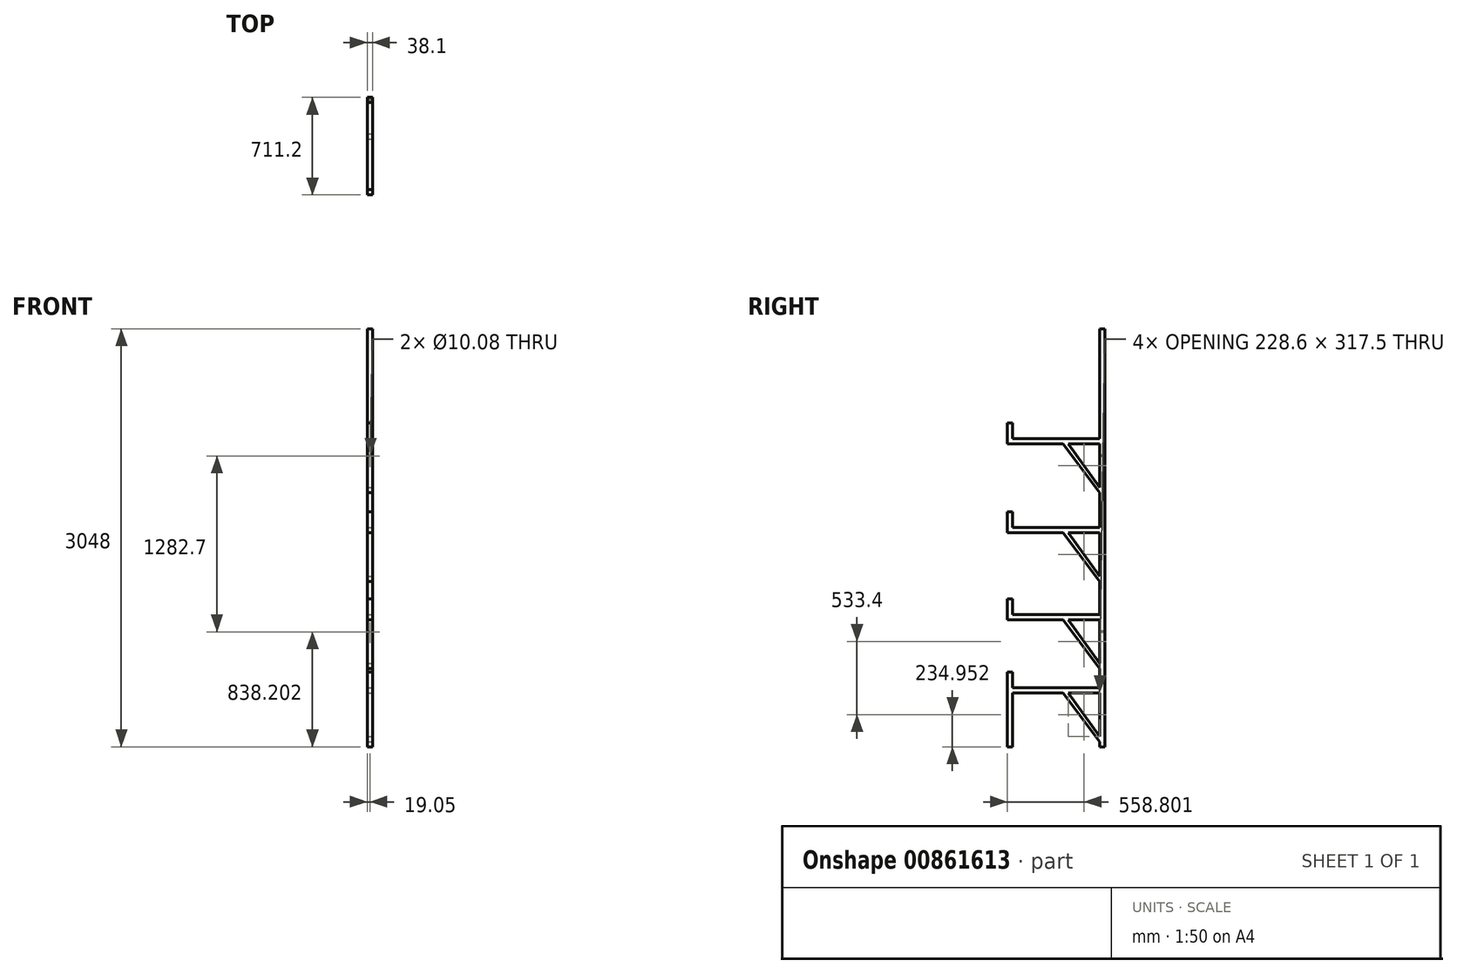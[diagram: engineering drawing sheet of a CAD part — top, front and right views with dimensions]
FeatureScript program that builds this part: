
annotation { "Feature Type Name" : "Feature", "Feature Type Description" : "" }
export const myFeature = defineFeature(function(context is Context, id is Id, definition is map)
    precondition{}
    {
        {
            var Q0;
            Q0=qCreatedBy(makeId("Right.planeOp"),FACE);
            var sketch = newSketch(context, id + "F0", { "sketchPlane" : qUnion([Q0])});
            skLineSegment(sketch, "E0.bottom", {"start": v(-10.09, 2961.46) * mm, "end": v(28.01, 2961.46) * mm});
            skLineSegment(sketch, "E0.top", {"start": v(-10.09, -86.54) * mm, "end": v(28.01, -86.54) * mm});
            skLineSegment(sketch, "E0.left", {"start": v(-10.09, 2961.46) * mm, "end": v(-10.09, -86.54) * mm});
            skLineSegment(sketch, "E0.right", {"start": v(28.01, 2961.46) * mm, "end": v(28.01, -86.54) * mm});
            skSolve(sketch);
        }
        {
            var Q0;
            Q0 = qSketchRegion(id + "F0", true);
            extrude(context, id + "F1", {"entities" : qUnion([Q0]), "depth" : 38.1 * mm, "offsetDistance" : 25.4 * mm});
        }
        {
            var Q0;
            Q0=makeQuery(id+"F1.opExtrude","SWEPT_FACE",FACE,{"disambiguationData":[OSD([sQuery(id+"F0.wireOp",EDGE,"E0.left")])]});
            var sketch = newSketch(context, id + "F2", { "sketchPlane" : qUnion([Q0])});
            skLineSegment(sketch, "E1.bottom", {"start": v(0, 2161.36) * mm, "end": v(38.1, 2161.36) * mm});
            skLineSegment(sketch, "E1.top", {"start": v(0, 2123.26) * mm, "end": v(38.1, 2123.26) * mm});
            skLineSegment(sketch, "E1.left", {"start": v(0, 2161.36) * mm, "end": v(0, 2123.26) * mm});
            skLineSegment(sketch, "E1.right", {"start": v(38.1, 2161.36) * mm, "end": v(38.1, 2123.26) * mm});
            skLineSegment(sketch, "E2.bottom", {"start": v(0, 1513.66) * mm, "end": v(38.1, 1513.66) * mm});
            skLineSegment(sketch, "E2.top", {"start": v(0, 1475.56) * mm, "end": v(38.1, 1475.56) * mm});
            skLineSegment(sketch, "E2.left", {"start": v(0, 1513.66) * mm, "end": v(0, 1475.56) * mm});
            skLineSegment(sketch, "E2.right", {"start": v(38.1, 1513.66) * mm, "end": v(38.1, 1475.56) * mm});
            skLineSegment(sketch, "E3.bottom", {"start": v(0, 878.66) * mm, "end": v(38.1, 878.66) * mm});
            skLineSegment(sketch, "E3.top", {"start": v(0, 840.56) * mm, "end": v(38.1, 840.56) * mm});
            skLineSegment(sketch, "E3.left", {"start": v(0, 878.66) * mm, "end": v(0, 840.56) * mm});
            skLineSegment(sketch, "E3.right", {"start": v(38.1, 878.66) * mm, "end": v(38.1, 840.56) * mm});
            skLineSegment(sketch, "E4.bottom", {"start": v(0, 345.26) * mm, "end": v(38.1, 345.26) * mm});
            skLineSegment(sketch, "E4.top", {"start": v(0, 307.16) * mm, "end": v(38.1, 307.16) * mm});
            skLineSegment(sketch, "E4.left", {"start": v(0, 345.26) * mm, "end": v(0, 307.16) * mm});
            skLineSegment(sketch, "E4.right", {"start": v(38.1, 345.26) * mm, "end": v(38.1, 307.16) * mm});
            skSolve(sketch);
        }
        {
            var Q0;
            Q0 = qSketchRegion(id + "F2", true);
            extrude(context, id + "F3", {"entities" : qUnion([Q0]), "operationType" : NewBodyOperationType.ADD, "depth" : 673.1 * mm, "offsetDistance" : 25.4 * mm});
        }
        {
            var Q0;
            Q0=makeQuery(id+"F3.opExtrude","SWEPT_FACE",FACE,{"disambiguationData":[OSD([sQuery(id+"F2.wireOp",EDGE,"E1.bottom")])]});
            var sketch = newSketch(context, id + "F4", { "sketchPlane" : qUnion([Q0])});
            skLineSegment(sketch, "E5.bottom", {"start": v(38.1, -683.19) * mm, "end": v(0, -683.19) * mm});
            skLineSegment(sketch, "E5.top", {"start": v(38.1, -645.09) * mm, "end": v(0, -645.09) * mm});
            skLineSegment(sketch, "E5.left", {"start": v(38.1, -683.19) * mm, "end": v(38.1, -645.09) * mm});
            skLineSegment(sketch, "E5.right", {"start": v(0, -683.19) * mm, "end": v(0, -645.09) * mm});
            skSolve(sketch);
        }
        {
            var Q0;
            Q0 = qSketchRegion(id + "F4", true);
            extrude(context, id + "F5", {"entities" : qUnion([Q0]), "operationType" : NewBodyOperationType.ADD, "depth" : 114.3 * mm, "offsetDistance" : 25.4 * mm});
        }
        {
            var Q0;
            Q0=makeQuery(id+"F3.opExtrude","SWEPT_FACE",FACE,{"disambiguationData":[OSD([sQuery(id+"F2.wireOp",EDGE,"E2.bottom")])]});
            var sketch = newSketch(context, id + "F6", { "sketchPlane" : qUnion([Q0])});
            skLineSegment(sketch, "E6.bottom", {"start": v(38.1, -683.19) * mm, "end": v(0, -683.19) * mm});
            skLineSegment(sketch, "E6.top", {"start": v(38.1, -645.09) * mm, "end": v(0, -645.09) * mm});
            skLineSegment(sketch, "E6.left", {"start": v(38.1, -683.19) * mm, "end": v(38.1, -645.09) * mm});
            skLineSegment(sketch, "E6.right", {"start": v(0, -683.19) * mm, "end": v(0, -645.09) * mm});
            skSolve(sketch);
        }
        {
            var Q0;
            Q0 = qSketchRegion(id + "F6", true);
            extrude(context, id + "F7", {"entities" : qUnion([Q0]), "operationType" : NewBodyOperationType.ADD, "depth" : 114.3 * mm, "offsetDistance" : 25.4 * mm});
        }
        {
            var Q0;
            Q0=makeQuery(id+"F3.opExtrude","SWEPT_FACE",FACE,{"disambiguationData":[OSD([sQuery(id+"F2.wireOp",EDGE,"E3.bottom")])]});
            var sketch = newSketch(context, id + "F8", { "sketchPlane" : qUnion([Q0])});
            skLineSegment(sketch, "E7.bottom", {"start": v(38.1, -683.19) * mm, "end": v(0, -683.19) * mm});
            skLineSegment(sketch, "E7.top", {"start": v(38.1, -645.09) * mm, "end": v(0, -645.09) * mm});
            skLineSegment(sketch, "E7.left", {"start": v(38.1, -683.19) * mm, "end": v(38.1, -645.09) * mm});
            skLineSegment(sketch, "E7.right", {"start": v(0, -683.19) * mm, "end": v(0, -645.09) * mm});
            skSolve(sketch);
        }
        {
            var Q0;
            Q0 = qSketchRegion(id + "F8", true);
            extrude(context, id + "F9", {"entities" : qUnion([Q0]), "operationType" : NewBodyOperationType.ADD, "depth" : 114.3 * mm, "offsetDistance" : 25.4 * mm});
        }
        {
            var Q0;
            Q0=makeQuery(id+"F3.opExtrude","SWEPT_FACE",FACE,{"disambiguationData":[OSD([sQuery(id+"F2.wireOp",EDGE,"E4.bottom")])]});
            var sketch = newSketch(context, id + "F10", { "sketchPlane" : qUnion([Q0])});
            skLineSegment(sketch, "E8.bottom", {"start": v(38.1, -683.19) * mm, "end": v(0, -683.19) * mm});
            skLineSegment(sketch, "E8.top", {"start": v(38.1, -645.09) * mm, "end": v(0, -645.09) * mm});
            skLineSegment(sketch, "E8.left", {"start": v(38.1, -683.19) * mm, "end": v(38.1, -645.09) * mm});
            skLineSegment(sketch, "E8.right", {"start": v(0, -683.19) * mm, "end": v(0, -645.09) * mm});
            skSolve(sketch);
        }
        {
            var Q0;
            Q0 = qSketchRegion(id + "F10", true);
            extrude(context, id + "F11", {"entities" : qUnion([Q0]), "operationType" : NewBodyOperationType.ADD, "depth" : 114.3 * mm, "offsetDistance" : 25.4 * mm});
        }
        {
            var Q0;
            Q0=makeQuery(id+"F3.opExtrude","SWEPT_FACE",FACE,{"disambiguationData":[OSD([sQuery(id+"F2.wireOp",EDGE,"E4.top")])]});
            var sketch = newSketch(context, id + "F12", { "sketchPlane" : qUnion([Q0])});
            skLineSegment(sketch, "E9.bottom", {"start": v(38.1, 683.19) * mm, "end": v(0, 683.19) * mm});
            skLineSegment(sketch, "E9.top", {"start": v(38.1, 645.09) * mm, "end": v(0, 645.09) * mm});
            skLineSegment(sketch, "E9.left", {"start": v(38.1, 683.19) * mm, "end": v(38.1, 645.09) * mm});
            skLineSegment(sketch, "E9.right", {"start": v(0, 683.19) * mm, "end": v(0, 645.09) * mm});
            skSolve(sketch);
        }
        {
            var Q0;
            Q0 = qSketchRegion(id + "F12", true);
            var Q1;
            Q1=makeQuery(id+"F1.opExtrude","SWEPT_FACE",FACE,{"disambiguationData":[OSD([sQuery(id+"F0.wireOp",EDGE,"E0.top")])]});
            extrude(context, id + "F13", {"entities" : qUnion([Q0]), "operationType" : NewBodyOperationType.ADD, "endBound" : BoundingType.UP_TO_SURFACE, "depth" : 25.4 * mm, "endBoundEntityFace" : qUnion([Q1]), "offsetDistance" : 25.4 * mm});
        }
        {
            var Q0;
            Q0=makeQuery(id+"F13.boolean.opBoolean","MERGE",FACE,{"derivedFrom":[makeQuery(id+"F11.boolean.opBoolean","MERGE",FACE,{"derivedFrom":[makeQuery(id+"F9.boolean.opBoolean","MERGE",FACE,{"derivedFrom":[makeQuery(id+"F7.boolean.opBoolean","MERGE",FACE,{"derivedFrom":[makeQuery(id+"F5.boolean.opBoolean","MERGE",FACE,{"derivedFrom":[makeQuery(id+"F3.boolean.opBoolean","MERGE",FACE,{"derivedFrom":[makeQuery(id+"F1.opExtrude","CAP_FACE",FACE,{"disambiguationData":[OSD([sQuery(id+"F0.wireOp",EDGE,"E0.bottom"),sQuery(id+"F0.wireOp",EDGE,"E0.top"),sQuery(id+"F0.wireOp",EDGE,"E0.left"),sQuery(id+"F0.wireOp",EDGE,"E0.right")])],"isStart":false}),makeQuery(id+"F3.opExtrude","SWEPT_FACE",FACE,{"disambiguationData":[OSD([sQuery(id+"F2.wireOp",EDGE,"E1.right")])]}),makeQuery(id+"F3.opExtrude","SWEPT_FACE",FACE,{"disambiguationData":[OSD([sQuery(id+"F2.wireOp",EDGE,"E2.right")])]}),makeQuery(id+"F3.opExtrude","SWEPT_FACE",FACE,{"disambiguationData":[OSD([sQuery(id+"F2.wireOp",EDGE,"E3.right")])]}),makeQuery(id+"F3.opExtrude","SWEPT_FACE",FACE,{"disambiguationData":[OSD([sQuery(id+"F2.wireOp",EDGE,"E4.right")])]})]}),makeQuery(id+"F5.opExtrude","SWEPT_FACE",FACE,{"disambiguationData":[OSD([sQuery(id+"F4.wireOp",EDGE,"E5.left")])]})]}),makeQuery(id+"F7.opExtrude","SWEPT_FACE",FACE,{"disambiguationData":[OSD([sQuery(id+"F6.wireOp",EDGE,"E6.left")])]})]}),makeQuery(id+"F9.opExtrude","SWEPT_FACE",FACE,{"disambiguationData":[OSD([sQuery(id+"F8.wireOp",EDGE,"E7.left")])]})]}),makeQuery(id+"F11.opExtrude","SWEPT_FACE",FACE,{"disambiguationData":[OSD([sQuery(id+"F10.wireOp",EDGE,"E8.left")])]})]}),makeQuery(id+"F13.opExtrude","SWEPT_FACE",FACE,{"disambiguationData":[OSD([sQuery(id+"F12.wireOp",EDGE,"E9.left")])]})]});
            var sketch = newSketch(context, id + "F14", { "sketchPlane" : qUnion([Q0])});
            skLineSegment(sketch, "E10", {"start": v(-10.09, 1767.66) * mm, "end": v(-276.79, 2123.26) * mm});
            skLineSegment(sketch, "E11", {"start": v(-276.79, 2123.26) * mm, "end": v(-238.69, 2123.26) * mm});
            skLineSegment(sketch, "E12", {"start": v(-238.69, 2123.26) * mm, "end": v(-10.09, 1805.76) * mm});
            skLineSegment(sketch, "E13", {"start": v(-10.09, 1805.76) * mm, "end": v(-10.09, 1767.66) * mm});
            skLineSegment(sketch, "E14", {"start": v(-10.09, 1119.96) * mm, "end": v(-276.79, 1475.56) * mm});
            skLineSegment(sketch, "E15", {"start": v(-276.79, 1475.56) * mm, "end": v(-238.69, 1475.56) * mm});
            skLineSegment(sketch, "E16", {"start": v(-238.69, 1475.56) * mm, "end": v(-10.09, 1158.06) * mm});
            skLineSegment(sketch, "E17", {"start": v(-10.09, 1158.06) * mm, "end": v(-10.09, 1119.96) * mm});
            skLineSegment(sketch, "E18", {"start": v(-276.79, 840.56) * mm, "end": v(-10.09, 484.96) * mm});
            skLineSegment(sketch, "E19", {"start": v(-10.09, 484.96) * mm, "end": v(-10.09, 523.06) * mm});
            skLineSegment(sketch, "E20", {"start": v(-10.09, 523.06) * mm, "end": v(-238.69, 840.56) * mm});
            skLineSegment(sketch, "E21", {"start": v(-238.69, 840.56) * mm, "end": v(-276.79, 840.56) * mm});
            skLineSegment(sketch, "E22", {"start": v(-276.79, 307.16) * mm, "end": v(-10.09, -48.44) * mm});
            skLineSegment(sketch, "E23", {"start": v(-10.09, -48.44) * mm, "end": v(-10.09, -10.34) * mm});
            skLineSegment(sketch, "E24", {"start": v(-10.09, -10.34) * mm, "end": v(-238.69, 307.16) * mm});
            skLineSegment(sketch, "E25", {"start": v(-238.69, 307.16) * mm, "end": v(-276.79, 307.16) * mm});
            skSolve(sketch);
        }
        {
            var Q0;
            Q0 = qSketchRegion(id + "F14", true);
            extrude(context, id + "F15", {"entities" : qUnion([Q0]), "operationType" : NewBodyOperationType.ADD, "oppositeDirection" : true, "depth" : 38.1 * mm, "offsetDistance" : 25.4 * mm});
        }
        {
            var Q0;
            {var subQ6=makeQuery(id+"F3.opExtrude","SWEPT_FACE",FACE,{"disambiguationData":[OSD([sQuery(id+"F2.wireOp",EDGE,"E1.top")])]});var subQ12=sQuery(id+"F0.wireOp",EDGE,"E0.left");Q0=makeQuery(id+"F15.boolean.opBoolean","SPLIT",FACE,{"disambiguationData":[TD([subQ6])],"derivedFrom":makeQuery(id+"F3.boolean.opBoolean","SPLIT",FACE,{"disambiguationData":[TD([subQ6])],"derivedFrom":makeQuery(id+"F1.opExtrude","SWEPT_FACE",FACE,{"disambiguationData":[OSD([subQ12])]})})});}
            var sketch = newSketch(context, id + "F16", { "sketchPlane" : qUnion([Q0])});
            skPoint(sketch, "E26", {"position": v(19.05, 2034.36) * mm});
            skPoint(sketch, "E26.positionSnap0", {"position": v(19.05, 2123.26) * mm});
            skPoint(sketch, "E27", {"position": v(19.05, 751.66) * mm});
            skSolve(sketch);
        }
        {
            var Q0;
            Q0=sQuery(id+"F16.wireOp",VERTEX,"E26");
            var Q1;
            Q1=sQuery(id+"F16.wireOp",VERTEX,"E27");
            var Q2;
            Q2=makeQuery(id+"F1.opExtrude","SWEPT_BODY",BODY,{"disambiguationData":[OSD([sQuery(id+"F0.wireOp",EDGE,"E0.bottom"),sQuery(id+"F0.wireOp",EDGE,"E0.top"),sQuery(id+"F0.wireOp",EDGE,"E0.left"),sQuery(id+"F0.wireOp",EDGE,"E0.right")])]});
            hole(context, id + "F17", {"style" : HoleStyle.SIMPLE, "endStyle" : HoleEndStyle.THROUGH, "standardTappedOrClearance" : lookupTablePath({ "fit" : "Normal (ASME)", "standard" : "ANSI", "size" : "3/8", "type" : "Clearance" }), "standardBlindInLast" : lookupTablePath({ "fit" : "Free", "standard" : "ANSI", "size" : "3/8", "type" : "Clearance" }), "holeDiameter" : 10.08 * mm, "majorDiameter" : 6.35 * mm, "isTappedThrough" : true, "tappedDepth" : 12.7 * mm, "tapClearance" : 3, "locations" : qUnion([Q0, Q1]), "scope" : qUnion([Q2])});
        }
    });
